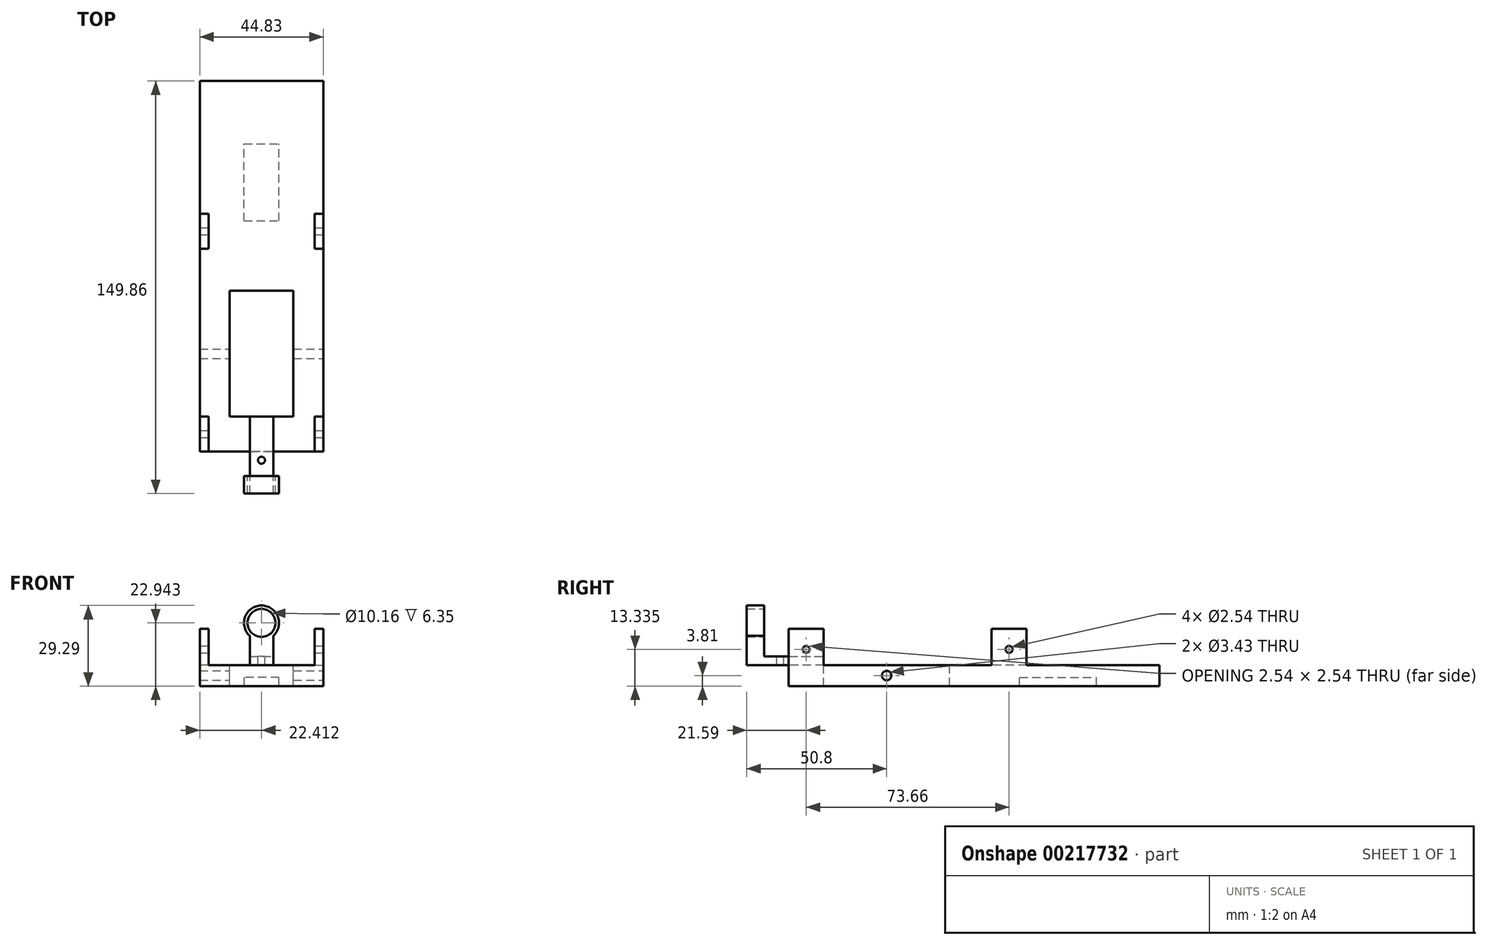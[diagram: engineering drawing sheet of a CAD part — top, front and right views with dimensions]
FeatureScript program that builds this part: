
annotation { "Feature Type Name" : "Feature", "Feature Type Description" : "" }
export const myFeature = defineFeature(function(context is Context, id is Id, definition is map)
    precondition{}
    {
        {
            var Q0;
            Q0=qCreatedBy(makeId("Front.planeOp"),FACE);
            var sketch = newSketch(context, id + "F0", { "sketchPlane" : qUnion([Q0])});
            skLineSegment(sketch, "E0.bottom", {"start": v(0, 0) * mm, "end": v(8.48, 0) * mm});
            skLineSegment(sketch, "E0.top", {"start": v(0, 3.18) * mm, "end": v(8.48, 3.18) * mm});
            skLineSegment(sketch, "E0.left", {"start": v(0, 0) * mm, "end": v(0, 3.18) * mm});
            skLineSegment(sketch, "E0.right", {"start": v(8.48, 0) * mm, "end": v(8.48, 3.18) * mm});
            skSolve(sketch);
        }
        {
            var Q0;
            Q0 = qSketchRegion(id + "F0", true);
            extrude(context, id + "F1", {"entities" : qUnion([Q0]), "depth" : 12.7 * mm});
        }
        {
            var Q0;
            Q0=makeQuery(id+"F1.opExtrude","CAP_FACE",FACE,{"disambiguationData":[OSD([sQuery(id+"F0.wireOp",EDGE,"E0.bottom"),sQuery(id+"F0.wireOp",EDGE,"E0.top"),sQuery(id+"F0.wireOp",EDGE,"E0.left"),sQuery(id+"F0.wireOp",EDGE,"E0.right")])],"isStart":true});
            var sketch = newSketch(context, id + "F2", { "sketchPlane" : qUnion([Q0])});
            skLineSegment(sketch, "E1", {"start": v(-8.48, 0) * mm, "end": v(-13.77, 0) * mm});
            skLineSegment(sketch, "E2", {"start": v(-8.48, 0) * mm, "end": v(-8.48, 3.18) * mm});
            skLineSegment(sketch, "E3", {"start": v(-8.48, 3.18) * mm, "end": v(0, 3.18) * mm});
            skLineSegment(sketch, "E4", {"start": v(0, 3.18) * mm, "end": v(0, 0) * mm});
            skPoint(sketch, "E5.orphan", {"position": v(-4.24, 0) * mm});
            skLineSegment(sketch, "E6", {"start": v(-4.24, -7.62) * mm, "end": v(-12.18, -7.62) * mm});
            skLineSegment(sketch, "E7", {"start": v(-12.18, -7.62) * mm, "end": v(-26.66, -7.62) * mm});
            skLineSegment(sketch, "E8", {"start": v(-26.66, -7.62) * mm, "end": v(-26.66, 13.2) * mm});
            skLineSegment(sketch, "E9", {"start": v(-26.66, 13.2) * mm, "end": v(-23.48, 13.2) * mm});
            skLineSegment(sketch, "E10", {"start": v(-23.48, 13.2) * mm, "end": v(-23.48, 0) * mm});
            skLineSegment(sketch, "E11", {"start": v(-23.48, 0) * mm, "end": v(-13.77, 0) * mm});
            skLineSegment(sketch, "E12.MirrorCS", {"start": v(-4.24, -7.62) * mm, "end": v(3.7, -7.62) * mm});
            skLineSegment(sketch, "E13.MirrorCS", {"start": v(15, 0) * mm, "end": v(5.28, 0) * mm});
            skLineSegment(sketch, "E14.MirrorCS", {"start": v(3.7, -7.62) * mm, "end": v(18.17, -7.62) * mm});
            skLineSegment(sketch, "E15.MirrorCS", {"start": v(18.17, 13.2) * mm, "end": v(15, 13.2) * mm});
            skLineSegment(sketch, "E16.MirrorCS", {"start": v(18.17, -7.62) * mm, "end": v(18.17, 13.2) * mm});
            skLineSegment(sketch, "E17.MirrorCS", {"start": v(15, 13.2) * mm, "end": v(15, 0) * mm});
            skLineSegment(sketch, "E18", {"start": v(0, 0) * mm, "end": v(5.28, 0) * mm});
            skSolve(sketch);
        }
        {
            var Q0;
            Q0 = qSketchRegion(id + "F2", true);
            extrude(context, id + "F3", {"entities" : qUnion([Q0]), "operationType" : NewBodyOperationType.ADD, "depth" : 8.9 * mm, "hasSecondDirection" : true, "secondDirectionOppositeDirection" : true, "secondDirectionDepth" : 3.8 * mm});
        }
        {
            var Q0;
            Q0=makeQuery(id+"F1.opExtrude","CAP_FACE",FACE,{"disambiguationData":[OSD([sQuery(id+"F0.wireOp",EDGE,"E0.bottom"),sQuery(id+"F0.wireOp",EDGE,"E0.top"),sQuery(id+"F0.wireOp",EDGE,"E0.left"),sQuery(id+"F0.wireOp",EDGE,"E0.right")])],"isStart":false});
            var sketch = newSketch(context, id + "F4", { "sketchPlane" : qUnion([Q0])});
            skCircle(sketch, "E19", {"center": v(4.24, 15.32) * mm, "radius": 5.08 * mm});
            skArc(sketch, "E20", {"start": v(8.48, 10.6) * mm, "mid": v(4.24, 21.67) * mm, "end": v(0, 10.6) * mm});
            skLineSegment(sketch, "E21.bottom", {"start": v(8.48, 0) * mm, "end": v(0, 0) * mm});
            skLineSegment(sketch, "E21.left", {"start": v(8.48, 0) * mm, "end": v(8.48, 10.6) * mm});
            skLineSegment(sketch, "E21.right", {"start": v(0, 0) * mm, "end": v(0, 10.6) * mm});
            skSolve(sketch);
        }
        {
            var Q0;
            Q0 = qSketchRegion(id + "F4", true);
            extrude(context, id + "F5", {"entities" : qUnion([Q0]), "operationType" : NewBodyOperationType.ADD, "depth" : 6.35 * mm});
        }
        {
            var Q0;
            Q0=makeQuery(id+"F3.boolean.opBoolean","MERGE",FACE,{"derivedFrom":[makeQuery(id+"F1.opExtrude","SWEPT_FACE",FACE,{"disambiguationData":[OSD([sQuery(id+"F0.wireOp",EDGE,"E0.top")])]}),makeQuery(id+"F3.opExtrude","SWEPT_FACE",FACE,{"disambiguationData":[OSD([sQuery(id+"F2.wireOp",EDGE,"E3")])]})]});
            var sketch = newSketch(context, id + "F6", { "sketchPlane" : qUnion([Q0])});
            skCircle(sketch, "E22", {"center": v(4.24, -6.95) * mm, "radius": 1.27 * mm});
            skPoint(sketch, "E22.centerSnap0", {"position": v(4.24, -12.7) * mm});
            skSolve(sketch);
        }
        {
            var Q0;
            Q0 = qSketchRegion(id + "F6", true);
            extrude(context, id + "F7", {"entities" : qUnion([Q0]), "operationType" : NewBodyOperationType.REMOVE, "oppositeDirection" : true, "depth" : 25.4 * mm});
        }
        {
            var Q0;
            Q0=makeQuery(id+"F3.opExtrude","SWEPT_FACE",FACE,{"disambiguationData":[OSD([sQuery(id+"F2.wireOp",EDGE,"E8")])]});
            var sketch = newSketch(context, id + "F8", { "sketchPlane" : qUnion([Q0])});
            skCircle(sketch, "E23", {"center": v(2.54, 5.72) * mm, "radius": 1.27 * mm});
            skLineSegment(sketch, "E24", {"start": v(-3.81, 13.2) * mm, "end": v(-3.81, 2.8) * mm});
            skLineSegment(sketch, "E25", {"start": v(8.89, 13.2) * mm, "end": v(8.89, -1.78) * mm});
            skPoint(sketch, "E25.endSnap0", {"position": v(8.89, 2.8) * mm});
            skLineSegment(sketch, "E26", {"start": v(-3.81, 13.2) * mm, "end": v(-3.81, -1.78) * mm});
            skLineSegment(sketch, "E27", {"start": v(-3.81, -1.78) * mm, "end": v(8.89, -1.78) * mm});
            skSolve(sketch);
        }
        {
            var Q0;
            Q0 = qSketchRegion(id + "F8", true);
            extrude(context, id + "F9", {"entities" : qUnion([Q0]), "operationType" : NewBodyOperationType.REMOVE, "oppositeDirection" : true, "depth" : 124.4 * mm});
        }
        {
            var Q0;
            Q0=makeQuery(id+"F3.opExtrude","CAP_FACE",FACE,{"disambiguationData":[OSD([sQuery(id+"F2.wireOp",EDGE,"E1"),sQuery(id+"F2.wireOp",EDGE,"E2"),sQuery(id+"F2.wireOp",EDGE,"E3"),sQuery(id+"F2.wireOp",EDGE,"E4"),sQuery(id+"F2.wireOp",EDGE,"E6"),sQuery(id+"F2.wireOp",EDGE,"E7"),sQuery(id+"F2.wireOp",EDGE,"E8"),sQuery(id+"F2.wireOp",EDGE,"E9"),sQuery(id+"F2.wireOp",EDGE,"E10"),sQuery(id+"F2.wireOp",EDGE,"E11"),sQuery(id+"F2.wireOp",EDGE,"E12.MirrorCS"),sQuery(id+"F2.wireOp",EDGE,"E13.MirrorCS"),sQuery(id+"F2.wireOp",EDGE,"E14.MirrorCS"),sQuery(id+"F2.wireOp",EDGE,"E15.MirrorCS"),sQuery(id+"F2.wireOp",EDGE,"E16.MirrorCS"),sQuery(id+"F2.wireOp",EDGE,"E17.MirrorCS"),sQuery(id+"F2.wireOp",EDGE,"E18")])],"isStart":false});
            var sketch = newSketch(context, id + "F10", { "sketchPlane" : qUnion([Q0])});
            skLineSegment(sketch, "E28", {"start": v(-4.24, 3.18) * mm, "end": v(-4.24, -7.62) * mm});
            skLineSegment(sketch, "E29", {"start": v(-4.24, -7.62) * mm, "end": v(-10.6, -7.62) * mm});
            skLineSegment(sketch, "E30", {"start": v(-10.6, -7.62) * mm, "end": v(-14.56, -7.62) * mm});
            skLineSegment(sketch, "E31", {"start": v(-14.56, -7.62) * mm, "end": v(-15.83, -7.62) * mm});
            skLineSegment(sketch, "E32.MirrorCS", {"start": v(-4.24, -7.62) * mm, "end": v(2.1, -7.62) * mm});
            skLineSegment(sketch, "E33.MirrorCS", {"start": v(2.1, -7.62) * mm, "end": v(6.08, -7.62) * mm});
            skLineSegment(sketch, "E34.MirrorCS", {"start": v(6.08, -7.62) * mm, "end": v(7.35, -7.62) * mm});
            skLineSegment(sketch, "E35.bottom", {"start": v(-15.83, -7.62) * mm, "end": v(-26.66, -7.62) * mm});
            skLineSegment(sketch, "E35.top", {"start": v(-15.83, 0) * mm, "end": v(-26.66, 0) * mm});
            skLineSegment(sketch, "E35.left", {"start": v(-15.83, -7.62) * mm, "end": v(-15.83, 0) * mm});
            skLineSegment(sketch, "E35.right", {"start": v(-26.66, -7.62) * mm, "end": v(-26.66, 0) * mm});
            skLineSegment(sketch, "E36.bottom", {"start": v(7.35, -7.62) * mm, "end": v(18.17, -7.62) * mm});
            skLineSegment(sketch, "E36.top", {"start": v(7.35, 0) * mm, "end": v(18.17, 0) * mm});
            skLineSegment(sketch, "E36.left", {"start": v(7.35, -7.62) * mm, "end": v(7.35, 0) * mm});
            skLineSegment(sketch, "E36.right", {"start": v(18.17, -7.62) * mm, "end": v(18.17, 0) * mm});
            skSolve(sketch);
        }
        {
            var Q0;
            Q0 = qSketchRegion(id + "F10", true);
            extrude(context, id + "F11", {"entities" : qUnion([Q0]), "operationType" : NewBodyOperationType.ADD, "depth" : 45.72 * mm});
        }
        {
            var Q0;
            Q0=makeQuery(id+"F11.opExtrude","CAP_FACE",FACE,{"disambiguationData":[OSD([sQuery(id+"F10.wireOp",EDGE,"E36.bottom"),sQuery(id+"F10.wireOp",EDGE,"E36.top"),sQuery(id+"F10.wireOp",EDGE,"E36.left"),sQuery(id+"F10.wireOp",EDGE,"E36.right")])],"isStart":false});
            var sketch = newSketch(context, id + "F12", { "sketchPlane" : qUnion([Q0])});
            skLineSegment(sketch, "E37", {"start": v(18.17, -7.62) * mm, "end": v(-26.66, -7.62) * mm});
            skLineSegment(sketch, "E38", {"start": v(18.17, -7.62) * mm, "end": v(18.17, 0) * mm});
            skLineSegment(sketch, "E39", {"start": v(18.17, 0) * mm, "end": v(-26.66, 0) * mm});
            skLineSegment(sketch, "E40", {"start": v(-26.66, 0) * mm, "end": v(-26.66, -7.62) * mm});
            skSolve(sketch);
        }
        {
            var Q0;
            Q0 = qSketchRegion(id + "F12", true);
            extrude(context, id + "F13", {"entities" : qUnion([Q0]), "operationType" : NewBodyOperationType.ADD, "depth" : 76.2 * mm});
        }
        {
            var Q0;
            Q0=makeQuery(id+"F13.boolean.opBoolean","MERGE",FACE,{"derivedFrom":[makeQuery(id+"F11.boolean.opBoolean","MERGE",FACE,{"derivedFrom":[makeQuery(id+"F3.opExtrude","SWEPT_FACE",FACE,{"disambiguationData":[OSD([sQuery(id+"F2.wireOp",EDGE,"E8")])]}),makeQuery(id+"F11.opExtrude","SWEPT_FACE",FACE,{"disambiguationData":[OSD([sQuery(id+"F10.wireOp",EDGE,"E35.right")])]})]}),makeQuery(id+"F13.opExtrude","SWEPT_FACE",FACE,{"disambiguationData":[OSD([sQuery(id+"F12.wireOp",EDGE,"E40")])]})]});
            var sketch = newSketch(context, id + "F14", { "sketchPlane" : qUnion([Q0])});
            skLineSegment(sketch, "E41", {"start": v(8.89, 0) * mm, "end": v(31.75, 0) * mm});
            skCircle(sketch, "E42", {"center": v(31.75, -3.8) * mm, "radius": 1.71 * mm});
            skSolve(sketch);
        }
        {
            var Q0;
            Q0 = qSketchRegion(id + "F14", true);
            extrude(context, id + "F15", {"entities" : qUnion([Q0]), "operationType" : NewBodyOperationType.REMOVE, "oppositeDirection" : true, "depth" : 51.64 * mm});
        }
        {
            var Q0;
            Q0=makeQuery(id+"F13.boolean.opBoolean","MERGE",FACE,{"derivedFrom":[makeQuery(id+"F11.boolean.opBoolean","MERGE",FACE,{"derivedFrom":[makeQuery(id+"F3.opExtrude","SWEPT_FACE",FACE,{"disambiguationData":[OSD([sQuery(id+"F2.wireOp",EDGE,"E8")])]}),makeQuery(id+"F11.opExtrude","SWEPT_FACE",FACE,{"disambiguationData":[OSD([sQuery(id+"F10.wireOp",EDGE,"E35.right")])]})]}),makeQuery(id+"F13.opExtrude","SWEPT_FACE",FACE,{"disambiguationData":[OSD([sQuery(id+"F12.wireOp",EDGE,"E40")])]})]});
            var sketch = newSketch(context, id + "F16", { "sketchPlane" : qUnion([Q0])});
            skLineSegment(sketch, "E43", {"start": v(69.85, 0) * mm, "end": v(69.85, 14.99) * mm});
            skLineSegment(sketch, "E44", {"start": v(69.85, 14.99) * mm, "end": v(82.55, 14.99) * mm});
            skLineSegment(sketch, "E45", {"start": v(82.55, 14.99) * mm, "end": v(82.55, 0) * mm});
            skLineSegment(sketch, "E46", {"start": v(82.55, 0) * mm, "end": v(69.85, 0) * mm});
            skSolve(sketch);
        }
        {
            var Q0;
            Q0 = qSketchRegion(id + "F16", true);
            extrude(context, id + "F17", {"entities" : qUnion([Q0]), "operationType" : NewBodyOperationType.ADD, "oppositeDirection" : true, "depth" : 3.17 * mm});
        }
        {
            var Q0;
            Q0=makeQuery(id+"F13.boolean.opBoolean","MERGE",FACE,{"derivedFrom":[makeQuery(id+"F11.boolean.opBoolean","MERGE",FACE,{"derivedFrom":[makeQuery(id+"F3.opExtrude","SWEPT_FACE",FACE,{"disambiguationData":[OSD([sQuery(id+"F2.wireOp",EDGE,"E16.MirrorCS")])]}),makeQuery(id+"F11.opExtrude","SWEPT_FACE",FACE,{"disambiguationData":[OSD([sQuery(id+"F10.wireOp",EDGE,"E36.right")])]})]}),makeQuery(id+"F13.opExtrude","SWEPT_FACE",FACE,{"disambiguationData":[OSD([sQuery(id+"F12.wireOp",EDGE,"E38")])]})]});
            var sketch = newSketch(context, id + "F18", { "sketchPlane" : qUnion([Q0])});
            skLineSegment(sketch, "E47", {"start": v(-69.85, 0) * mm, "end": v(-69.85, 14.99) * mm});
            skLineSegment(sketch, "E48", {"start": v(-69.85, 14.99) * mm, "end": v(-82.55, 14.99) * mm});
            skLineSegment(sketch, "E49", {"start": v(-82.55, 14.99) * mm, "end": v(-82.55, 0) * mm});
            skLineSegment(sketch, "E50", {"start": v(-82.55, 0) * mm, "end": v(-69.85, 0) * mm});
            skSolve(sketch);
        }
        {
            var Q0;
            Q0 = qSketchRegion(id + "F18", true);
            extrude(context, id + "F19", {"entities" : qUnion([Q0]), "operationType" : NewBodyOperationType.ADD, "oppositeDirection" : true, "depth" : 3.17 * mm});
        }
        {
            var Q0;
            Q0=makeQuery(id+"F17.boolean.opBoolean","MERGE",FACE,{"derivedFrom":[makeQuery(id+"F13.boolean.opBoolean","MERGE",FACE,{"derivedFrom":[makeQuery(id+"F11.boolean.opBoolean","MERGE",FACE,{"derivedFrom":[makeQuery(id+"F3.opExtrude","SWEPT_FACE",FACE,{"disambiguationData":[OSD([sQuery(id+"F2.wireOp",EDGE,"E8")])]}),makeQuery(id+"F11.opExtrude","SWEPT_FACE",FACE,{"disambiguationData":[OSD([sQuery(id+"F10.wireOp",EDGE,"E35.right")])]})]}),makeQuery(id+"F13.opExtrude","SWEPT_FACE",FACE,{"disambiguationData":[OSD([sQuery(id+"F12.wireOp",EDGE,"E40")])]})]}),makeQuery(id+"F17.opExtrude","CAP_FACE",FACE,{"disambiguationData":[OSD([sQuery(id+"F16.wireOp",EDGE,"E43"),sQuery(id+"F16.wireOp",EDGE,"E44"),sQuery(id+"F16.wireOp",EDGE,"E45"),sQuery(id+"F16.wireOp",EDGE,"E46")])],"isStart":true})]});
            var sketch = newSketch(context, id + "F20", { "sketchPlane" : qUnion([Q0])});
            skLineSegment(sketch, "E51", {"start": v(82.55, 13.2) * mm, "end": v(82.55, 14.99) * mm});
            skLineSegment(sketch, "E52", {"start": v(82.55, 14.99) * mm, "end": v(69.85, 14.99) * mm});
            skLineSegment(sketch, "E53", {"start": v(69.85, 14.99) * mm, "end": v(69.85, 13.2) * mm});
            skCircle(sketch, "E54", {"center": v(76.2, 5.72) * mm, "radius": 1.27 * mm});
            skLineSegment(sketch, "E55", {"start": v(69.85, 13.2) * mm, "end": v(82.55, 13.2) * mm});
            skSolve(sketch);
        }
        {
            var Q0;
            Q0 = qSketchRegion(id + "F20", true);
            extrude(context, id + "F21", {"entities" : qUnion([Q0]), "operationType" : NewBodyOperationType.REMOVE, "oppositeDirection" : true, "depth" : 51.05 * mm});
        }
        {
            var Q0;
            Q0=makeQuery(id+"F13.opExtrude","CAP_FACE",FACE,{"disambiguationData":[OSD([sQuery(id+"F12.wireOp",EDGE,"E37"),sQuery(id+"F12.wireOp",EDGE,"E38"),sQuery(id+"F12.wireOp",EDGE,"E39"),sQuery(id+"F12.wireOp",EDGE,"E40")])],"isStart":false});
            var sketch = newSketch(context, id + "F22", { "sketchPlane" : qUnion([Q0])});
            skLineSegment(sketch, "E56", {"start": v(-4.24, -7.62) * mm, "end": v(-10.6, -7.62) * mm});
            skLineSegment(sketch, "E57", {"start": v(-10.6, -7.62) * mm, "end": v(-10.6, -4.44) * mm});
            skLineSegment(sketch, "E58", {"start": v(-10.6, -4.44) * mm, "end": v(2.1, -4.44) * mm});
            skLineSegment(sketch, "E59", {"start": v(2.1, -4.44) * mm, "end": v(2.1, -7.62) * mm});
            skLineSegment(sketch, "E60", {"start": v(2.1, -7.62) * mm, "end": v(-4.24, -7.62) * mm});
            skSolve(sketch);
        }
        {
            var Q0;
            Q0 = qSketchRegion(id + "F22", true);
            extrude(context, id + "F23", {"entities" : qUnion([Q0]), "operationType" : NewBodyOperationType.REMOVE, "oppositeDirection" : true, "depth" : 50.8 * mm});
        }
        {
            var Q0;
            Q0=makeQuery(id+"F13.opExtrude","CAP_FACE",FACE,{"disambiguationData":[OSD([sQuery(id+"F12.wireOp",EDGE,"E37"),sQuery(id+"F12.wireOp",EDGE,"E38"),sQuery(id+"F12.wireOp",EDGE,"E39"),sQuery(id+"F12.wireOp",EDGE,"E40")])],"isStart":false});
            var sketch = newSketch(context, id + "F24", { "sketchPlane" : qUnion([Q0])});
            skLineSegment(sketch, "E61.bottom", {"start": v(2.1, -4.44) * mm, "end": v(-10.6, -4.44) * mm});
            skLineSegment(sketch, "E61.top", {"start": v(2.1, -7.62) * mm, "end": v(-10.6, -7.62) * mm});
            skLineSegment(sketch, "E61.left", {"start": v(2.1, -4.44) * mm, "end": v(2.1, -7.62) * mm});
            skLineSegment(sketch, "E61.right", {"start": v(-10.6, -4.44) * mm, "end": v(-10.6, -7.62) * mm});
            skSolve(sketch);
        }
        {
            var Q0;
            Q0 = qSketchRegion(id + "F24", true);
            extrude(context, id + "F25", {"entities" : qUnion([Q0]), "operationType" : NewBodyOperationType.ADD, "oppositeDirection" : true, "depth" : 22.86 * mm});
        }
    });
